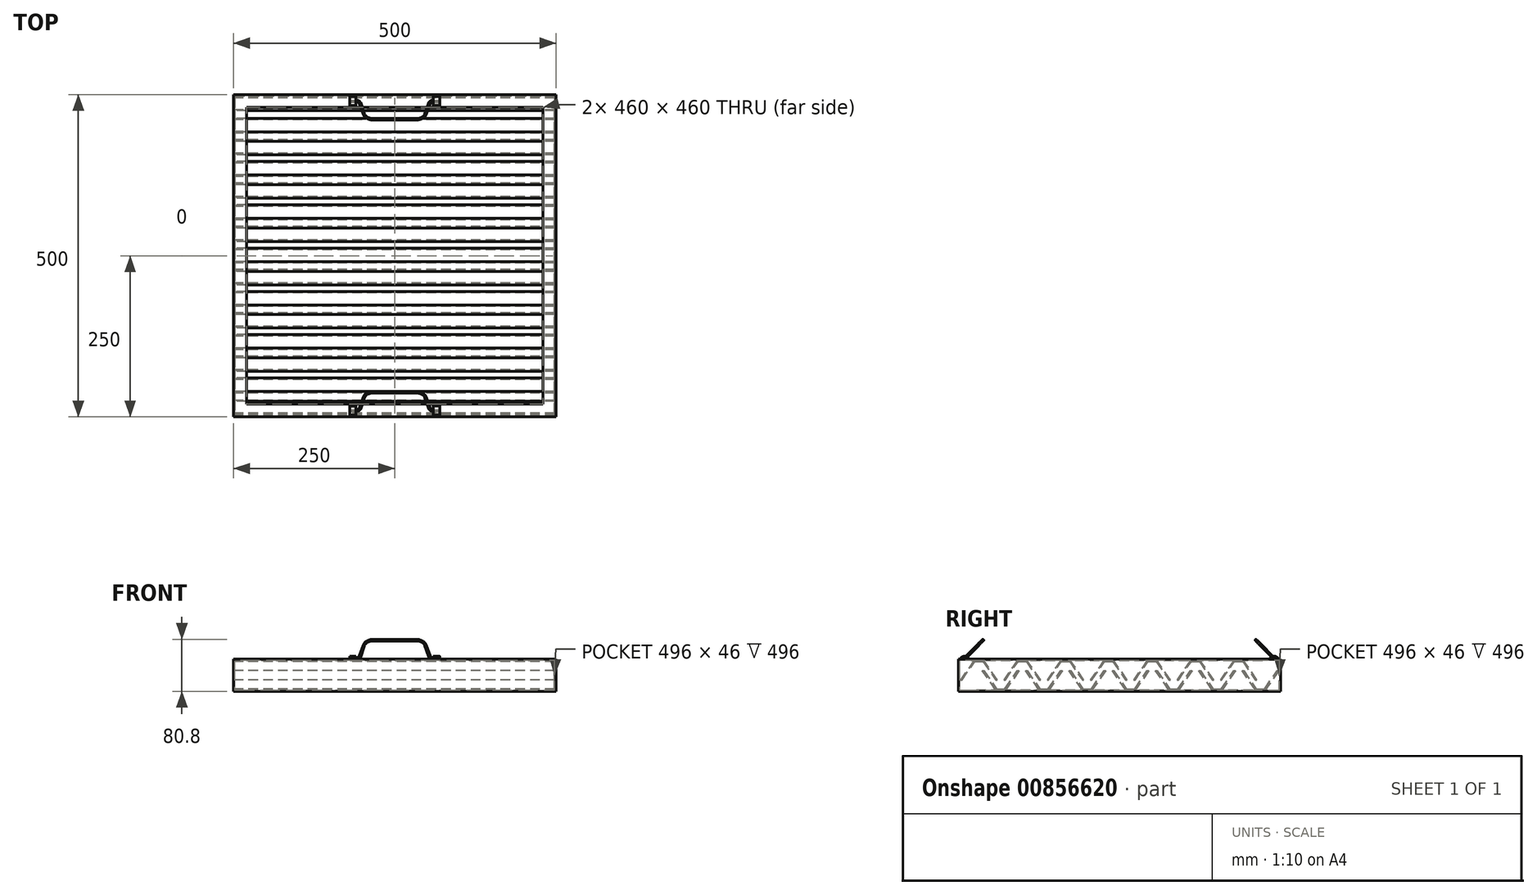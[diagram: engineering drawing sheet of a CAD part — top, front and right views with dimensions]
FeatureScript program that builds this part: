
annotation { "Feature Type Name" : "Feature", "Feature Type Description" : "" }
export const myFeature = defineFeature(function(context is Context, id is Id, definition is map)
    precondition{}
    {
        {
            var Q0;
            Q0=qCreatedBy(makeId("Right.planeOp"),FACE);
            var sketch = newSketch(context, id + "F0", { "sketchPlane" : qUnion([Q0])});
            skLineSegment(sketch, "E0", {"start": v(230, 10) * mm, "end": v(250, 10) * mm});
            skLineSegment(sketch, "E1", {"start": v(250, 10) * mm, "end": v(250, -40) * mm});
            skLineSegment(sketch, "E2", {"start": v(250, -40) * mm, "end": v(230, -40) * mm});
            skLineSegment(sketch, "E3", {"start": v(230, -40) * mm, "end": v(230, -38) * mm});
            skLineSegment(sketch, "E4", {"start": v(230, -38) * mm, "end": v(248, -38) * mm});
            skLineSegment(sketch, "E5", {"start": v(248, -38) * mm, "end": v(248, 8) * mm});
            skLineSegment(sketch, "E6", {"start": v(248, 8) * mm, "end": v(230, 8) * mm});
            skLineSegment(sketch, "E7", {"start": v(230, 8) * mm, "end": v(230, 10) * mm});
            skSolve(sketch);
        }
        {
            var Q0;
            Q0=qCreatedBy(makeId("Top.planeOp"),FACE);
            var sketch = newSketch(context, id + "F1", { "sketchPlane" : qUnion([Q0])});
            skLineSegment(sketch, "E8.bottom", {"start": v(-250, 250) * mm, "end": v(250, 250) * mm});
            skLineSegment(sketch, "E8.top", {"start": v(-250, -250) * mm, "end": v(250, -250) * mm});
            skLineSegment(sketch, "E8.left", {"start": v(-250, 250) * mm, "end": v(-250, -250) * mm});
            skLineSegment(sketch, "E8.right", {"start": v(250, 250) * mm, "end": v(250, -250) * mm});
            skPoint(sketch, "E8.middle", {"position": v(0, 0) * mm});
            skSolve(sketch);
        }
        {
            var Q0;
            Q0=makeQuery(id+"F0.imprint","IMPRINT",FACE,{"disambiguationData":[TD([[makeQuery(id+"F0.imprint","IMPRINT",EDGE,{"derivedFrom":sQuery(id+"F0.wireOp",EDGE,"E0")}),-1.0]])]});
            var Q1;
            Q1=sQuery(id+"F1.wireOp",EDGE,"E8.bottom");
            var Q2;
            Q2=sQuery(id+"F1.wireOp",EDGE,"E8.right");
            var Q3;
            Q3=sQuery(id+"F1.wireOp",EDGE,"E8.top");
            var Q4;
            Q4=sQuery(id+"F1.wireOp",EDGE,"E8.left");
            sweep(context, id + "F2", {"profiles" : qUnion([Q0]), "path" : qUnion([Q1, Q2, Q3, Q4])});
        }
        {
            var Q0;
            Q0=makeQuery(id+"F2.opSweep","SWEPT_FACE",FACE,{"disambiguationData":[OSD([sQuery(id+"F0.wireOp",EDGE,"E5"),sQuery(id+"F1.wireOp",EDGE,"E8.left")])]});
            var sketch = newSketch(context, id + "F3", { "sketchPlane" : qUnion([Q0])});
            skLineSegment(sketch, "E9", {"start": v(-246.5, -22) * mm, "end": v(-225.5, 8) * mm});
            skLineSegment(sketch, "E10", {"start": v(-225.5, 8) * mm, "end": v(-210.5, 8) * mm});
            skLineSegment(sketch, "E11", {"start": v(-210.5, 8) * mm, "end": v(-189.49, -22) * mm});
            skLineSegment(sketch, "E12", {"start": v(-189.49, -22) * mm, "end": v(-191.93, -22) * mm});
            skLineSegment(sketch, "E13", {"start": v(-191.93, -22) * mm, "end": v(-211.53, 6) * mm});
            skLineSegment(sketch, "E14", {"start": v(-211.53, 6) * mm, "end": v(-224.45, 6) * mm});
            skLineSegment(sketch, "E15", {"start": v(-224.45, 6) * mm, "end": v(-244.06, -22) * mm});
            skLineSegment(sketch, "E16", {"start": v(-244.06, -22) * mm, "end": v(-246.5, -22) * mm});
            skLineSegment(sketch, "E17", {"start": v(-212.72, -8) * mm, "end": v(-191.71, -38) * mm});
            skLineSegment(sketch, "E18", {"start": v(-191.71, -38) * mm, "end": v(-176.71, -38) * mm});
            skLineSegment(sketch, "E19", {"start": v(-176.71, -38) * mm, "end": v(-155.7, -8) * mm});
            skLineSegment(sketch, "E20", {"start": v(-155.7, -8) * mm, "end": v(-158.15, -8) * mm});
            skLineSegment(sketch, "E21", {"start": v(-158.15, -8) * mm, "end": v(-177.75, -36) * mm});
            skLineSegment(sketch, "E22", {"start": v(-177.75, -36) * mm, "end": v(-190.67, -36) * mm});
            skLineSegment(sketch, "E23", {"start": v(-190.67, -36) * mm, "end": v(-210.28, -8) * mm});
            skLineSegment(sketch, "E24", {"start": v(-210.28, -8) * mm, "end": v(-212.72, -8) * mm});
            skLineSegment(sketch, "E25.1.0.0", {"start": v(-109.56, -38) * mm, "end": v(-88.56, -8) * mm});
            skLineSegment(sketch, "E25.1.0.1", {"start": v(-91, -8) * mm, "end": v(-110.6, -36) * mm});
            skLineSegment(sketch, "E25.1.0.2", {"start": v(-144.39, 6) * mm, "end": v(-157.3, 6) * mm});
            skLineSegment(sketch, "E25.1.0.3", {"start": v(-179.35, -22) * mm, "end": v(-158.34, 8) * mm});
            skLineSegment(sketch, "E25.1.0.4", {"start": v(-143.34, 8) * mm, "end": v(-122.34, -22) * mm});
            skLineSegment(sketch, "E25.1.0.5", {"start": v(-124.78, -22) * mm, "end": v(-144.39, 6) * mm});
            skLineSegment(sketch, "E25.1.0.6", {"start": v(-110.6, -36) * mm, "end": v(-123.52, -36) * mm});
            skLineSegment(sketch, "E25.1.0.7", {"start": v(-157.3, 6) * mm, "end": v(-176.9, -22) * mm});
            skLineSegment(sketch, "E25.1.0.8", {"start": v(-123.52, -36) * mm, "end": v(-143.13, -8) * mm});
            skLineSegment(sketch, "E25.1.0.9", {"start": v(-145.57, -8) * mm, "end": v(-124.56, -38) * mm});
            skLineSegment(sketch, "E25.1.0.10", {"start": v(-124.56, -38) * mm, "end": v(-109.56, -38) * mm});
            skLineSegment(sketch, "E25.1.0.11", {"start": v(-158.34, 8) * mm, "end": v(-143.34, 8) * mm});
            skLineSegment(sketch, "E25.1.0.12", {"start": v(-176.9, -22) * mm, "end": v(-179.35, -22) * mm});
            skLineSegment(sketch, "E25.1.0.13", {"start": v(-88.56, -8) * mm, "end": v(-91, -8) * mm});
            skLineSegment(sketch, "E25.1.0.14", {"start": v(-143.13, -8) * mm, "end": v(-145.57, -8) * mm});
            skLineSegment(sketch, "E25.1.0.15", {"start": v(-122.34, -22) * mm, "end": v(-124.78, -22) * mm});
            skLineSegment(sketch, "E25.2.0.0", {"start": v(-42.41, -38) * mm, "end": v(-21.4, -8) * mm});
            skLineSegment(sketch, "E25.2.0.1", {"start": v(-23.85, -8) * mm, "end": v(-43.46, -36) * mm});
            skLineSegment(sketch, "E25.2.0.2", {"start": v(-77.24, 6) * mm, "end": v(-90.15, 6) * mm});
            skLineSegment(sketch, "E25.2.0.3", {"start": v(-112.2, -22) * mm, "end": v(-91.2, 8) * mm});
            skLineSegment(sketch, "E25.2.0.4", {"start": v(-76.2, 8) * mm, "end": v(-55.19, -22) * mm});
            skLineSegment(sketch, "E25.2.0.5", {"start": v(-57.63, -22) * mm, "end": v(-77.24, 6) * mm});
            skLineSegment(sketch, "E25.2.0.6", {"start": v(-43.46, -36) * mm, "end": v(-56.37, -36) * mm});
            skLineSegment(sketch, "E25.2.0.7", {"start": v(-90.15, 6) * mm, "end": v(-109.76, -22) * mm});
            skLineSegment(sketch, "E25.2.0.8", {"start": v(-56.37, -36) * mm, "end": v(-75.98, -8) * mm});
            skLineSegment(sketch, "E25.2.0.9", {"start": v(-78.42, -8) * mm, "end": v(-57.41, -38) * mm});
            skLineSegment(sketch, "E25.2.0.10", {"start": v(-57.41, -38) * mm, "end": v(-42.41, -38) * mm});
            skLineSegment(sketch, "E25.2.0.11", {"start": v(-91.2, 8) * mm, "end": v(-76.2, 8) * mm});
            skLineSegment(sketch, "E25.2.0.12", {"start": v(-109.76, -22) * mm, "end": v(-112.2, -22) * mm});
            skLineSegment(sketch, "E25.2.0.13", {"start": v(-21.4, -8) * mm, "end": v(-23.85, -8) * mm});
            skLineSegment(sketch, "E25.2.0.14", {"start": v(-75.98, -8) * mm, "end": v(-78.42, -8) * mm});
            skLineSegment(sketch, "E25.2.0.15", {"start": v(-55.19, -22) * mm, "end": v(-57.63, -22) * mm});
            skLineSegment(sketch, "E25.3.0.0", {"start": v(24.74, -38) * mm, "end": v(45.74, -8) * mm});
            skLineSegment(sketch, "E25.3.0.1", {"start": v(43.3, -8) * mm, "end": v(23.7, -36) * mm});
            skLineSegment(sketch, "E25.3.0.2", {"start": v(-10.09, 6) * mm, "end": v(-23, 6) * mm});
            skLineSegment(sketch, "E25.3.0.3", {"start": v(-45.05, -22) * mm, "end": v(-24.05, 8) * mm});
            skLineSegment(sketch, "E25.3.0.4", {"start": v(-9.05, 8) * mm, "end": v(11.96, -22) * mm});
            skLineSegment(sketch, "E25.3.0.5", {"start": v(9.52, -22) * mm, "end": v(-10.09, 6) * mm});
            skLineSegment(sketch, "E25.3.0.6", {"start": v(23.7, -36) * mm, "end": v(10.78, -36) * mm});
            skLineSegment(sketch, "E25.3.0.7", {"start": v(-23, 6) * mm, "end": v(-42.61, -22) * mm});
            skLineSegment(sketch, "E25.3.0.8", {"start": v(10.78, -36) * mm, "end": v(-8.83, -8) * mm});
            skLineSegment(sketch, "E25.3.0.9", {"start": v(-11.27, -8) * mm, "end": v(9.74, -38) * mm});
            skLineSegment(sketch, "E25.3.0.10", {"start": v(9.74, -38) * mm, "end": v(24.74, -38) * mm});
            skLineSegment(sketch, "E25.3.0.11", {"start": v(-24.05, 8) * mm, "end": v(-9.05, 8) * mm});
            skLineSegment(sketch, "E25.3.0.12", {"start": v(-42.61, -22) * mm, "end": v(-45.05, -22) * mm});
            skLineSegment(sketch, "E25.3.0.13", {"start": v(45.74, -8) * mm, "end": v(43.3, -8) * mm});
            skLineSegment(sketch, "E25.3.0.14", {"start": v(-8.83, -8) * mm, "end": v(-11.27, -8) * mm});
            skLineSegment(sketch, "E25.3.0.15", {"start": v(11.96, -22) * mm, "end": v(9.52, -22) * mm});
            skLineSegment(sketch, "E25.4.0.0", {"start": v(91.88, -38) * mm, "end": v(112.9, -8) * mm});
            skLineSegment(sketch, "E25.4.0.1", {"start": v(110.45, -8) * mm, "end": v(90.84, -36) * mm});
            skLineSegment(sketch, "E25.4.0.2", {"start": v(57.06, 6) * mm, "end": v(44.14, 6) * mm});
            skLineSegment(sketch, "E25.4.0.3", {"start": v(22.1, -22) * mm, "end": v(43.1, 8) * mm});
            skLineSegment(sketch, "E25.4.0.4", {"start": v(58.1, 8) * mm, "end": v(79.1, -22) * mm});
            skLineSegment(sketch, "E25.4.0.5", {"start": v(76.67, -22) * mm, "end": v(57.06, 6) * mm});
            skLineSegment(sketch, "E25.4.0.6", {"start": v(90.84, -36) * mm, "end": v(77.93, -36) * mm});
            skLineSegment(sketch, "E25.4.0.7", {"start": v(44.14, 6) * mm, "end": v(24.54, -22) * mm});
            skLineSegment(sketch, "E25.4.0.8", {"start": v(77.93, -36) * mm, "end": v(58.32, -8) * mm});
            skLineSegment(sketch, "E25.4.0.9", {"start": v(55.88, -8) * mm, "end": v(76.88, -38) * mm});
            skLineSegment(sketch, "E25.4.0.10", {"start": v(76.88, -38) * mm, "end": v(91.88, -38) * mm});
            skLineSegment(sketch, "E25.4.0.11", {"start": v(43.1, 8) * mm, "end": v(58.1, 8) * mm});
            skLineSegment(sketch, "E25.4.0.12", {"start": v(24.54, -22) * mm, "end": v(22.1, -22) * mm});
            skLineSegment(sketch, "E25.4.0.13", {"start": v(112.9, -8) * mm, "end": v(110.45, -8) * mm});
            skLineSegment(sketch, "E25.4.0.14", {"start": v(58.32, -8) * mm, "end": v(55.88, -8) * mm});
            skLineSegment(sketch, "E25.4.0.15", {"start": v(79.1, -22) * mm, "end": v(76.67, -22) * mm});
            skLineSegment(sketch, "E25.5.0.0", {"start": v(159.03, -38) * mm, "end": v(180.04, -8) * mm});
            skLineSegment(sketch, "E25.5.0.1", {"start": v(177.6, -8) * mm, "end": v(158, -36) * mm});
            skLineSegment(sketch, "E25.5.0.2", {"start": v(124.21, 6) * mm, "end": v(111.3, 6) * mm});
            skLineSegment(sketch, "E25.5.0.3", {"start": v(89.25, -22) * mm, "end": v(110.25, 8) * mm});
            skLineSegment(sketch, "E25.5.0.4", {"start": v(125.25, 8) * mm, "end": v(146.26, -22) * mm});
            skLineSegment(sketch, "E25.5.0.5", {"start": v(143.82, -22) * mm, "end": v(124.21, 6) * mm});
            skLineSegment(sketch, "E25.5.0.6", {"start": v(158, -36) * mm, "end": v(145.08, -36) * mm});
            skLineSegment(sketch, "E25.5.0.7", {"start": v(111.3, 6) * mm, "end": v(91.69, -22) * mm});
            skLineSegment(sketch, "E25.5.0.8", {"start": v(145.08, -36) * mm, "end": v(125.47, -8) * mm});
            skLineSegment(sketch, "E25.5.0.9", {"start": v(123.03, -8) * mm, "end": v(144.03, -38) * mm});
            skLineSegment(sketch, "E25.5.0.10", {"start": v(144.03, -38) * mm, "end": v(159.03, -38) * mm});
            skLineSegment(sketch, "E25.5.0.11", {"start": v(110.25, 8) * mm, "end": v(125.25, 8) * mm});
            skLineSegment(sketch, "E25.5.0.12", {"start": v(91.69, -22) * mm, "end": v(89.25, -22) * mm});
            skLineSegment(sketch, "E25.5.0.13", {"start": v(180.04, -8) * mm, "end": v(177.6, -8) * mm});
            skLineSegment(sketch, "E25.5.0.14", {"start": v(125.47, -8) * mm, "end": v(123.03, -8) * mm});
            skLineSegment(sketch, "E25.5.0.15", {"start": v(146.26, -22) * mm, "end": v(143.82, -22) * mm});
            skLineSegment(sketch, "E25.6.0.0", {"start": v(226.18, -38) * mm, "end": v(247.19, -8) * mm});
            skLineSegment(sketch, "E25.6.0.1", {"start": v(244.75, -8) * mm, "end": v(225.14, -36) * mm});
            skLineSegment(sketch, "E25.6.0.2", {"start": v(191.36, 6) * mm, "end": v(178.44, 6) * mm});
            skLineSegment(sketch, "E25.6.0.3", {"start": v(156.4, -22) * mm, "end": v(177.4, 8) * mm});
            skLineSegment(sketch, "E25.6.0.4", {"start": v(192.4, 8) * mm, "end": v(213.4, -22) * mm});
            skLineSegment(sketch, "E25.6.0.5", {"start": v(210.97, -22) * mm, "end": v(191.36, 6) * mm});
            skLineSegment(sketch, "E25.6.0.6", {"start": v(225.14, -36) * mm, "end": v(212.22, -36) * mm});
            skLineSegment(sketch, "E25.6.0.7", {"start": v(178.44, 6) * mm, "end": v(158.84, -22) * mm});
            skLineSegment(sketch, "E25.6.0.8", {"start": v(212.22, -36) * mm, "end": v(192.62, -8) * mm});
            skLineSegment(sketch, "E25.6.0.9", {"start": v(190.18, -8) * mm, "end": v(211.18, -38) * mm});
            skLineSegment(sketch, "E25.6.0.10", {"start": v(211.18, -38) * mm, "end": v(226.18, -38) * mm});
            skLineSegment(sketch, "E25.6.0.11", {"start": v(177.4, 8) * mm, "end": v(192.4, 8) * mm});
            skLineSegment(sketch, "E25.6.0.12", {"start": v(158.84, -22) * mm, "end": v(156.4, -22) * mm});
            skLineSegment(sketch, "E25.6.0.13", {"start": v(247.19, -8) * mm, "end": v(244.75, -8) * mm});
            skLineSegment(sketch, "E25.6.0.14", {"start": v(192.62, -8) * mm, "end": v(190.18, -8) * mm});
            skLineSegment(sketch, "E25.6.0.15", {"start": v(213.4, -22) * mm, "end": v(210.97, -22) * mm});
            skLineSegment(sketch, "E25.direction1", {"start": v(-246.5, -22) * mm, "end": v(-179.35, -22) * mm, "construction": true});
            skSolve(sketch);
        }
        {
            var Q0;
            Q0 = qSketchRegion(id + "F3", true);
            var Q1;
            Q1=makeQuery(id+"F2.opSweep","SWEPT_FACE",FACE,{"disambiguationData":[OSD([sQuery(id+"F0.wireOp",EDGE,"E5"),sQuery(id+"F1.wireOp",EDGE,"E8.right")])]});
            extrude(context, id + "F4", {"entities" : qUnion([Q0]), "endBound" : BoundingType.UP_TO_SURFACE, "depth" : 25 * mm, "endBoundEntityFace" : qUnion([Q1]), "offsetDistance" : 25 * mm});
        }
        {
            var Q0;
            Q0=qCreatedBy(makeId("Right.planeOp"),FACE);
            cPlane(context, id + "F5", {"entities" : qUnion([Q0]), "cplaneType" : CPlaneType.OFFSET, "offset" : 60 * mm, "width" : 150 * mm, "height" : 150 * mm});
        }
        {
            var Q0;
            Q0=qCreatedBy(id+"F5.planeOp",FACE);
            var sketch = newSketch(context, id + "F6", { "sketchPlane" : qUnion([Q0])});
            skLineSegment(sketch, "E26", {"start": v(247.5, 10) * mm, "end": v(243, 14.5) * mm});
            skLineSegment(sketch, "E27", {"start": v(243, 14.5) * mm, "end": v(237, 14.5) * mm});
            skLineSegment(sketch, "E28", {"start": v(237, 14.5) * mm, "end": v(232.5, 10) * mm});
            skLineSegment(sketch, "E29", {"start": v(232.5, 10) * mm, "end": v(234.62, 10) * mm});
            skLineSegment(sketch, "E30", {"start": v(234.62, 10) * mm, "end": v(237.62, 13) * mm});
            skLineSegment(sketch, "E31", {"start": v(237.62, 13) * mm, "end": v(242.38, 13) * mm});
            skLineSegment(sketch, "E32", {"start": v(242.38, 13) * mm, "end": v(245.38, 10) * mm});
            skLineSegment(sketch, "E33", {"start": v(245.38, 10) * mm, "end": v(247.5, 10) * mm});
            skLineSegment(sketch, "E34.MirrorCS", {"start": v(-232.5, 10) * mm, "end": v(-234.62, 10) * mm});
            skLineSegment(sketch, "E35.MirrorCS", {"start": v(-245.38, 10) * mm, "end": v(-247.5, 10) * mm});
            skLineSegment(sketch, "E36.MirrorCS", {"start": v(-234.62, 10) * mm, "end": v(-237.62, 13) * mm});
            skLineSegment(sketch, "E37.MirrorCS", {"start": v(-237, 14.5) * mm, "end": v(-232.5, 10) * mm});
            skLineSegment(sketch, "E38.MirrorCS", {"start": v(-237.62, 13) * mm, "end": v(-242.38, 13) * mm});
            skLineSegment(sketch, "E39.MirrorCS", {"start": v(-247.5, 10) * mm, "end": v(-243, 14.5) * mm});
            skLineSegment(sketch, "E40.MirrorCS", {"start": v(-242.38, 13) * mm, "end": v(-245.38, 10) * mm});
            skLineSegment(sketch, "E41.MirrorCS", {"start": v(-243, 14.5) * mm, "end": v(-237, 14.5) * mm});
            skSolve(sketch);
        }
        {
            var Q0;
            Q0 = qSketchRegion(id + "F6", true);
            extrude(context, id + "F7", {"entities" : qUnion([Q0]), "depth" : 10 * mm, "offsetDistance" : 25 * mm});
        }
        {
            var Q0;
            Q0=makeQuery(id+"F7.opExtrude","SWEPT_BODY",BODY,{"disambiguationData":[OSD([sQuery(id+"F6.wireOp",EDGE,"E34.MirrorCS"),sQuery(id+"F6.wireOp",EDGE,"E35.MirrorCS"),sQuery(id+"F6.wireOp",EDGE,"E36.MirrorCS"),sQuery(id+"F6.wireOp",EDGE,"E37.MirrorCS"),sQuery(id+"F6.wireOp",EDGE,"E38.MirrorCS"),sQuery(id+"F6.wireOp",EDGE,"E39.MirrorCS"),sQuery(id+"F6.wireOp",EDGE,"E40.MirrorCS"),sQuery(id+"F6.wireOp",EDGE,"E41.MirrorCS")])]});
            var Q1;
            Q1=makeQuery(id+"F7.opExtrude","SWEPT_BODY",BODY,{"disambiguationData":[OSD([sQuery(id+"F6.wireOp",EDGE,"E26"),sQuery(id+"F6.wireOp",EDGE,"E27"),sQuery(id+"F6.wireOp",EDGE,"E28"),sQuery(id+"F6.wireOp",EDGE,"E29"),sQuery(id+"F6.wireOp",EDGE,"E30"),sQuery(id+"F6.wireOp",EDGE,"E31"),sQuery(id+"F6.wireOp",EDGE,"E32"),sQuery(id+"F6.wireOp",EDGE,"E33")])]});
            var Q2;
            Q2=qCreatedBy(makeId("Right.planeOp"),FACE);
            mirror(context, id + "F8", {"operationType" : NewBodyOperationType.ADD, "entities" : qUnion([Q0, Q1]), "mirrorPlane" : qUnion([Q2])});
        }
        {
            var Q0;
            Q0=makeQuery(id+"F8.opPattern","COPY",EDGE,{"derivedFrom":makeQuery(id+"F7.opExtrude","SWEPT_EDGE",EDGE,{"disambiguationData":[OSD([sQuery(id+"F6.wireOp",EDGE,"E26"),sQuery(id+"F6.wireOp",EDGE,"E33")])]}),"instanceName":"1"});
            var Q1;
            Q1=makeQuery(id+"F8.opPattern","COPY",EDGE,{"derivedFrom":makeQuery(id+"F7.opExtrude","SWEPT_EDGE",EDGE,{"disambiguationData":[OSD([sQuery(id+"F6.wireOp",EDGE,"E26"),sQuery(id+"F6.wireOp",EDGE,"E27")])]}),"instanceName":"1"});
            var Q2;
            Q2=makeQuery(id+"F8.opPattern","COPY",EDGE,{"derivedFrom":makeQuery(id+"F7.opExtrude","SWEPT_EDGE",EDGE,{"disambiguationData":[OSD([sQuery(id+"F6.wireOp",EDGE,"E27"),sQuery(id+"F6.wireOp",EDGE,"E28")])]}),"instanceName":"1"});
            var Q3;
            Q3=makeQuery(id+"F8.opPattern","COPY",EDGE,{"derivedFrom":makeQuery(id+"F7.opExtrude","SWEPT_EDGE",EDGE,{"disambiguationData":[OSD([sQuery(id+"F6.wireOp",EDGE,"E28"),sQuery(id+"F6.wireOp",EDGE,"E29")])]}),"instanceName":"1"});
            var Q4;
            Q4=makeQuery(id+"F8.opPattern","COPY",EDGE,{"derivedFrom":makeQuery(id+"F7.opExtrude","SWEPT_EDGE",EDGE,{"disambiguationData":[OSD([sQuery(id+"F6.wireOp",EDGE,"E30"),sQuery(id+"F6.wireOp",EDGE,"E31")])]}),"instanceName":"1"});
            var Q5;
            Q5=makeQuery(id+"F8.opPattern","COPY",EDGE,{"derivedFrom":makeQuery(id+"F7.opExtrude","SWEPT_EDGE",EDGE,{"disambiguationData":[OSD([sQuery(id+"F6.wireOp",EDGE,"E31"),sQuery(id+"F6.wireOp",EDGE,"E32")])]}),"instanceName":"1"});
            var Q6;
            Q6=makeQuery(id+"F7.opExtrude","SWEPT_EDGE",EDGE,{"disambiguationData":[OSD([sQuery(id+"F6.wireOp",EDGE,"E26"),sQuery(id+"F6.wireOp",EDGE,"E33")])]});
            var Q7;
            Q7=makeQuery(id+"F7.opExtrude","SWEPT_EDGE",EDGE,{"disambiguationData":[OSD([sQuery(id+"F6.wireOp",EDGE,"E26"),sQuery(id+"F6.wireOp",EDGE,"E27")])]});
            var Q8;
            Q8=makeQuery(id+"F7.opExtrude","SWEPT_EDGE",EDGE,{"disambiguationData":[OSD([sQuery(id+"F6.wireOp",EDGE,"E27"),sQuery(id+"F6.wireOp",EDGE,"E28")])]});
            var Q9;
            Q9=makeQuery(id+"F7.opExtrude","SWEPT_EDGE",EDGE,{"disambiguationData":[OSD([sQuery(id+"F6.wireOp",EDGE,"E28"),sQuery(id+"F6.wireOp",EDGE,"E29")])]});
            var Q10;
            Q10=makeQuery(id+"F7.opExtrude","SWEPT_EDGE",EDGE,{"disambiguationData":[OSD([sQuery(id+"F6.wireOp",EDGE,"E30"),sQuery(id+"F6.wireOp",EDGE,"E31")])]});
            var Q11;
            Q11=makeQuery(id+"F7.opExtrude","SWEPT_EDGE",EDGE,{"disambiguationData":[OSD([sQuery(id+"F6.wireOp",EDGE,"E31"),sQuery(id+"F6.wireOp",EDGE,"E32")])]});
            var Q12;
            Q12=makeQuery(id+"F8.opPattern","COPY",EDGE,{"derivedFrom":makeQuery(id+"F7.opExtrude","SWEPT_EDGE",EDGE,{"disambiguationData":[OSD([sQuery(id+"F6.wireOp",EDGE,"E34.MirrorCS"),sQuery(id+"F6.wireOp",EDGE,"E37.MirrorCS")])]}),"instanceName":"1"});
            var Q13;
            Q13=makeQuery(id+"F8.opPattern","COPY",EDGE,{"derivedFrom":makeQuery(id+"F7.opExtrude","SWEPT_EDGE",EDGE,{"disambiguationData":[OSD([sQuery(id+"F6.wireOp",EDGE,"E37.MirrorCS"),sQuery(id+"F6.wireOp",EDGE,"E41.MirrorCS")])]}),"instanceName":"1"});
            var Q14;
            Q14=makeQuery(id+"F8.opPattern","COPY",EDGE,{"derivedFrom":makeQuery(id+"F7.opExtrude","SWEPT_EDGE",EDGE,{"disambiguationData":[OSD([sQuery(id+"F6.wireOp",EDGE,"E39.MirrorCS"),sQuery(id+"F6.wireOp",EDGE,"E41.MirrorCS")])]}),"instanceName":"1"});
            var Q15;
            Q15=makeQuery(id+"F8.opPattern","COPY",EDGE,{"derivedFrom":makeQuery(id+"F7.opExtrude","SWEPT_EDGE",EDGE,{"disambiguationData":[OSD([sQuery(id+"F6.wireOp",EDGE,"E35.MirrorCS"),sQuery(id+"F6.wireOp",EDGE,"E39.MirrorCS")])]}),"instanceName":"1"});
            var Q16;
            Q16=makeQuery(id+"F8.opPattern","COPY",EDGE,{"derivedFrom":makeQuery(id+"F7.opExtrude","SWEPT_EDGE",EDGE,{"disambiguationData":[OSD([sQuery(id+"F6.wireOp",EDGE,"E38.MirrorCS"),sQuery(id+"F6.wireOp",EDGE,"E40.MirrorCS")])]}),"instanceName":"1"});
            var Q17;
            Q17=makeQuery(id+"F8.opPattern","COPY",EDGE,{"derivedFrom":makeQuery(id+"F7.opExtrude","SWEPT_EDGE",EDGE,{"disambiguationData":[OSD([sQuery(id+"F6.wireOp",EDGE,"E36.MirrorCS"),sQuery(id+"F6.wireOp",EDGE,"E38.MirrorCS")])]}),"instanceName":"1"});
            var Q18;
            Q18=makeQuery(id+"F7.opExtrude","SWEPT_EDGE",EDGE,{"disambiguationData":[OSD([sQuery(id+"F6.wireOp",EDGE,"E34.MirrorCS"),sQuery(id+"F6.wireOp",EDGE,"E37.MirrorCS")])]});
            var Q19;
            Q19=makeQuery(id+"F7.opExtrude","SWEPT_EDGE",EDGE,{"disambiguationData":[OSD([sQuery(id+"F6.wireOp",EDGE,"E36.MirrorCS"),sQuery(id+"F6.wireOp",EDGE,"E38.MirrorCS")])]});
            var Q20;
            Q20=makeQuery(id+"F7.opExtrude","SWEPT_EDGE",EDGE,{"disambiguationData":[OSD([sQuery(id+"F6.wireOp",EDGE,"E37.MirrorCS"),sQuery(id+"F6.wireOp",EDGE,"E41.MirrorCS")])]});
            var Q21;
            Q21=makeQuery(id+"F7.opExtrude","SWEPT_EDGE",EDGE,{"disambiguationData":[OSD([sQuery(id+"F6.wireOp",EDGE,"E38.MirrorCS"),sQuery(id+"F6.wireOp",EDGE,"E40.MirrorCS")])]});
            var Q22;
            Q22=makeQuery(id+"F7.opExtrude","SWEPT_EDGE",EDGE,{"disambiguationData":[OSD([sQuery(id+"F6.wireOp",EDGE,"E39.MirrorCS"),sQuery(id+"F6.wireOp",EDGE,"E41.MirrorCS")])]});
            var Q23;
            Q23=makeQuery(id+"F7.opExtrude","SWEPT_EDGE",EDGE,{"disambiguationData":[OSD([sQuery(id+"F6.wireOp",EDGE,"E35.MirrorCS"),sQuery(id+"F6.wireOp",EDGE,"E39.MirrorCS")])]});
            fillet(context, id + "F9", {"entities" : qUnion([Q0, Q1, Q2, Q3, Q4, Q5, Q6, Q7, Q8, Q9, Q10, Q11, Q12, Q13, Q14, Q15, Q16, Q17, Q18, Q19, Q20, Q21, Q22, Q23]), "radius" : 5 * mm, "tangentPropagation" : true, "allowEdgeOverflow" : false});
        }
        {
            var Q0;
            Q0=makeQuery(id+"F2.opSweep","SWEPT_FACE",FACE,{"disambiguationData":[OSD([sQuery(id+"F0.wireOp",EDGE,"E0"),sQuery(id+"F1.wireOp",EDGE,"E8.right")])]});
            cPlane(context, id + "F10", {"entities" : qUnion([Q0]), "cplaneType" : CPlaneType.OFFSET, "offset" : 1.25 * mm, "width" : 150 * mm, "height" : 150 * mm});
        }
        {
            var Q0;
            Q0=qCreatedBy(makeId("Front.planeOp"),FACE);
            cPlane(context, id + "F11", {"entities" : qUnion([Q0]), "cplaneType" : CPlaneType.OFFSET, "offset" : 240 * mm, "oppositeDirection" : true, "width" : 150 * mm, "height" : 150 * mm});
        }
        {
            var Q0;
            Q0=qCreatedBy(id+"F11.planeOp",FACE);
            var Q1;
            Q1=qCreatedBy(id+"F10.planeOp",FACE);
            cPlane(context, id + "F12", {"entities" : qUnion([Q0, Q1]), "cplaneType" : CPlaneType.MID_PLANE, "offset" : 25 * mm, "width" : 150 * mm, "height" : 150 * mm});
        }
        {
            var Q0;
            Q0=qCreatedBy(id+"F12.planeOp",FACE);
            var sketch = newSketch(context, id + "F13", { "sketchPlane" : qUnion([Q0])});
            skLineSegment(sketch, "E42", {"start": v(70, -161.73) * mm, "end": v(58.9, -161.73) * mm});
            skLineSegment(sketch, "E43", {"start": v(54.05, -157.94) * mm, "end": v(47.84, -133.1) * mm});
            skLineSegment(sketch, "E44", {"start": v(33.29, -121.73) * mm, "end": v(-33.29, -121.73) * mm});
            skLineSegment(sketch, "E45", {"start": v(-47.84, -133.1) * mm, "end": v(-54.05, -157.94) * mm});
            skLineSegment(sketch, "E46", {"start": v(-58.9, -161.73) * mm, "end": v(-70, -161.73) * mm});
            skPoint(sketch, "E47.visualSharp", {"position": v(-55, -161.73) * mm});
            skArc(sketch, "E47.filletArc", {"start": v(-58.9, -161.73) * mm, "mid": v(-55.83, -160.67) * mm, "end": v(-54.05, -157.94) * mm});
            skPoint(sketch, "E48.visualSharp", {"position": v(55, -161.73) * mm});
            skArc(sketch, "E48.filletArc", {"start": v(54.05, -157.94) * mm, "mid": v(55.83, -160.67) * mm, "end": v(58.9, -161.73) * mm});
            skPoint(sketch, "E49.visualSharp", {"position": v(-45, -121.73) * mm});
            skArc(sketch, "E49.filletArc", {"start": v(-33.29, -121.73) * mm, "mid": v(-42.52, -124.9) * mm, "end": v(-47.84, -133.1) * mm});
            skPoint(sketch, "E50.visualSharp", {"position": v(45, -121.73) * mm});
            skArc(sketch, "E50.filletArc", {"start": v(47.84, -133.1) * mm, "mid": v(42.52, -124.9) * mm, "end": v(33.29, -121.73) * mm});
            skSolve(sketch);
        }
        {
            var Q0;
            Q0=qCreatedBy(makeId("Right.planeOp"),FACE);
            var sketch = newSketch(context, id + "F14", { "sketchPlane" : qUnion([Q0])});
            skCircle(sketch, "E51", {"center": v(211.7, 39.55) * mm, "radius": 1.25 * mm});
            skSolve(sketch);
        }
        {
            var Q0;
            Q0=makeQuery(id+"F14.imprint","IMPRINT",FACE,{"disambiguationData":[TD([[makeQuery(id+"F14.imprint","IMPRINT",EDGE,{"derivedFrom":sQuery(id+"F14.wireOp",EDGE,"E51")}),1.0]])]});
            var Q1;
            Q1=sQuery(id+"F13.wireOp",EDGE,"E44");
            var Q2;
            Q2=sQuery(id+"F13.wireOp",EDGE,"E49.filletArc");
            var Q3;
            Q3=sQuery(id+"F13.wireOp",EDGE,"E45");
            var Q4;
            Q4=sQuery(id+"F13.wireOp",EDGE,"E47.filletArc");
            var Q5;
            Q5=sQuery(id+"F13.wireOp",EDGE,"E46");
            var Q6;
            Q6=sQuery(id+"F13.wireOp",EDGE,"E50.filletArc");
            var Q7;
            Q7=sQuery(id+"F13.wireOp",EDGE,"E43");
            var Q8;
            Q8=sQuery(id+"F13.wireOp",EDGE,"E48.filletArc");
            var Q9;
            Q9=sQuery(id+"F13.wireOp",EDGE,"E42");
            sweep(context, id + "F15", {"profiles" : qUnion([Q0]), "path" : qUnion([Q1, Q2, Q3, Q4, Q5, Q6, Q7, Q8, Q9])});
        }
        {
            var Q0;
            Q0=makeQuery(id+"F15.opSweep","SWEPT_BODY",BODY,{"disambiguationData":[OSD([sQuery(id+"F13.wireOp",EDGE,"E42"),sQuery(id+"F14.wireOp",EDGE,"E51")])]});
            var Q1;
            Q1=qCreatedBy(makeId("Front.planeOp"),FACE);
            mirror(context, id + "F16", {"entities" : qUnion([Q0]), "mirrorPlane" : qUnion([Q1])});
        }
    });
